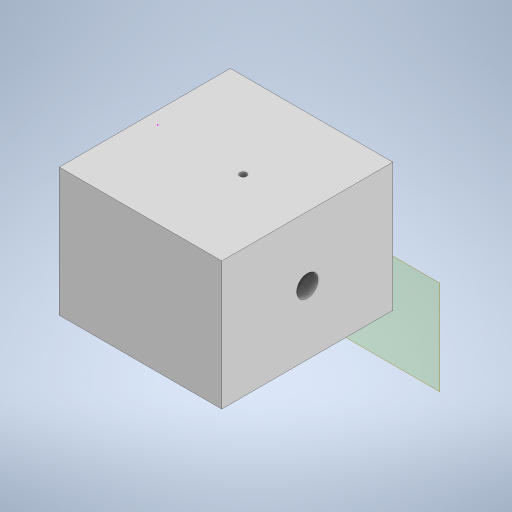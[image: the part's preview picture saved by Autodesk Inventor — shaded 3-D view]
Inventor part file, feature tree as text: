
AUTODESK INVENTOR PART (.ipt)
format: ipt  version: 2023 (Build 270158000, 158)  size: 288,768 bytes
history: native  units: mm
features: sketch x9, extrude x7, plane x6
ambient origin geometry x8: Origin, YZ Plane, XZ Plane, XY Plane, X Axis, Y Axis, Z Axis, Center Point
bodies: Body1 (feature_tree)
feature tree (22):
  plane  "Work Plane13"
  extrude  "Extrusion34"  Depth=40.0mm
  sketch  "Sketch46"  dims[d144=30.0mm d145=0.0mm d146=36.0mm]
  plane  "Work Plane11"
  extrude  "Extrusion35"  Depth=36.0mm
  sketch  "Sketch48"  dims[d150=0.0mm d151=0.0mm d156=20.0mm]
  extrude  "Extrusion36"  Depth=1.5mm
  plane  "Work Plane7"
  extrude  "Extrusion38"  Depth=20.0mm
  plane  "Work Plane4"
  extrude  "Extrusion39"  Depth=15.0mm TaperAngle=0.0deg
  plane  "Work Plane1"
  plane  "Work Plane6"
  extrude  "Extrusion42"  Depth=20.0mm
  extrude  "Extrusion44"  Depth=5.0mm
  sketch  "Sketch45"  dims[d142=38.0mm d143=40.0mm]
  sketch  "Sketch47"  dims[d147=30.0mm d148=-2.617994mm d149=1.5mm]
  sketch  "Sketch49"  dims[d157=15.0mm d158=15.0mm d159=0.0mm]
  sketch  "Sketch58"  dims[d160=4.0mm d161=20.0mm]
  sketch  "Sketch59"  dims[d162=35.0mm d163=0.0mm d172=5.0mm]
  sketch  "Sketch62"  dims[d173=0.0mm d174=0.0mm]
  sketch  "Sketch65"  dims[d177=5.0mm d178=0.0mm d49=0.5mm d50=0.872665mm d51=0.5mm d52=0.872665mm d130=0.5mm d131=0.872665mm d132=0.5mm d133=0.872665mm]
